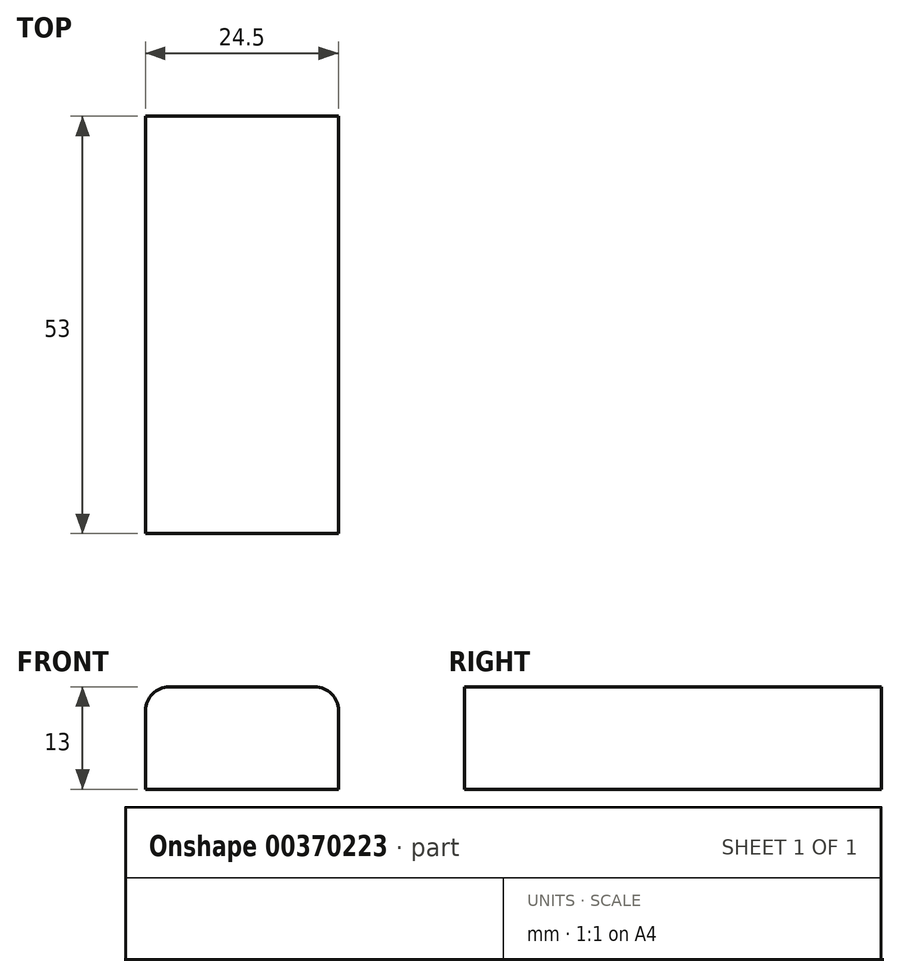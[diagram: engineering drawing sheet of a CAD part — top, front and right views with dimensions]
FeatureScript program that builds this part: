
annotation { "Feature Type Name" : "Feature", "Feature Type Description" : "" }
export const myFeature = defineFeature(function(context is Context, id is Id, definition is map)
    precondition{}
    {
        {
            var Q0;
            Q0=qCreatedBy(makeId("Front.planeOp"),FACE);
            var sketch = newSketch(context, id + "F0", { "sketchPlane" : qUnion([Q0])});
            skLineSegment(sketch, "E0.bottom", {"start": v(-56.58, 47.82) * mm, "end": v(-38.08, 47.82) * mm});
            skLineSegment(sketch, "E0.top", {"start": v(-59.58, 34.82) * mm, "end": v(-35.08, 34.82) * mm});
            skLineSegment(sketch, "E0.left", {"start": v(-59.58, 44.82) * mm, "end": v(-59.58, 34.82) * mm});
            skLineSegment(sketch, "E0.right", {"start": v(-35.08, 44.82) * mm, "end": v(-35.08, 34.82) * mm});
            skPoint(sketch, "E1.visualSharp", {"position": v(-59.58, 47.82) * mm});
            skArc(sketch, "E1.filletArc", {"start": v(-56.58, 47.82) * mm, "mid": v(-58.7, 46.94) * mm, "end": v(-59.58, 44.82) * mm});
            skPoint(sketch, "E2.visualSharp", {"position": v(-35.08, 47.82) * mm});
            skArc(sketch, "E2.filletArc", {"start": v(-35.08, 44.82) * mm, "mid": v(-35.96, 46.94) * mm, "end": v(-38.08, 47.82) * mm});
            skSolve(sketch);
        }
        {
            var Q0;
            Q0=makeQuery(id+"F0.imprint","IMPRINT",FACE,{"disambiguationData":[TD([[makeQuery(id+"F0.imprint","IMPRINT",EDGE,{"derivedFrom":sQuery(id+"F0.wireOp",EDGE,"E0.bottom")}),-1.0]])]});
            extrude(context, id + "F1", {"entities" : qUnion([Q0]), "depth" : 53 * mm});
        }
    });
